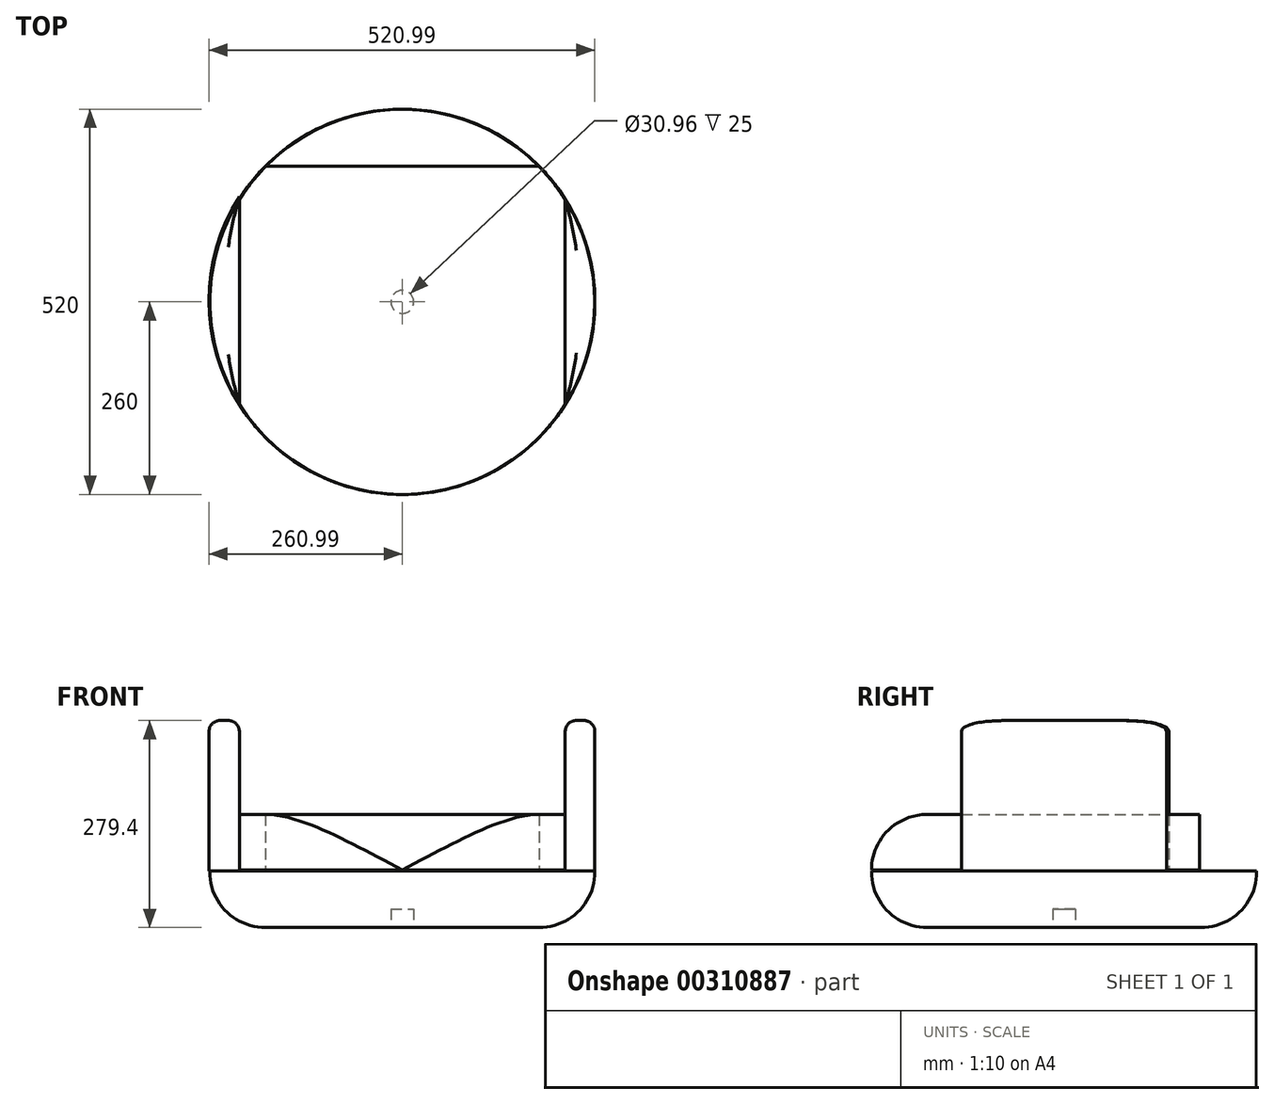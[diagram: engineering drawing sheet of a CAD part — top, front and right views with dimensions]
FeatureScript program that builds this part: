
annotation { "Feature Type Name" : "Feature", "Feature Type Description" : "" }
export const myFeature = defineFeature(function(context is Context, id is Id, definition is map)
    precondition{}
    {
        {
            var Q0;
            Q0=qCreatedBy(makeId("Front.planeOp"),FACE);
            var sketch = newSketch(context, id + "F0", { "sketchPlane" : qUnion([Q0])});
            skLineSegment(sketch, "E0.bottom", {"start": v(260, 38.1) * mm, "end": v(0, 38.1) * mm});
            skLineSegment(sketch, "E0.top", {"start": v(185, -38.1) * mm, "end": v(0, -38.1) * mm});
            skLineSegment(sketch, "E0.left", {"start": v(260, 38.1) * mm, "end": v(260, 36.9) * mm});
            skLineSegment(sketch, "E0.right", {"start": v(-260, 38.1) * mm, "end": v(-260, 36.9) * mm});
            skPoint(sketch, "E0.middle", {"position": v(0, 0) * mm});
            skPoint(sketch, "E1.visualSharp", {"position": v(260, -38.1) * mm});
            skArc(sketch, "E1.filletArc", {"start": v(185, -38.1) * mm, "mid": v(238.03, -16.13) * mm, "end": v(260, 36.9) * mm});
            skPoint(sketch, "E2.visualSharp", {"position": v(-260, -38.1) * mm});
            skLineSegment(sketch, "E3", {"start": v(0, 38.1) * mm, "end": v(0, -38.1) * mm});
            skPoint(sketch, "E2.filletArc.end.orphan", {"position": v(-185, -38.1) * mm});
            skSolve(sketch);
        }
        {
            var Q0;
            Q0=makeQuery(id+"F0.imprint","IMPRINT",FACE,{"disambiguationData":[TD([[makeQuery(id+"F0.imprint","IMPRINT",EDGE,{"derivedFrom":sQuery(id+"F0.wireOp",EDGE,"E0.bottom")}),1.0]])]});
            var Q1;
            Q1=sQuery(id+"F0.wireOp",EDGE,"E3");
            revolve(context, id + "F1", {"entities" : qUnion([Q0]), "axis" : qUnion([Q1]), "revolveType" : RevolveType.FULL});
        }
        {
            var Q0;
            Q0=qCreatedBy(makeId("Right.planeOp"),FACE);
            var sketch = newSketch(context, id + "F2", { "sketchPlane" : qUnion([Q0])});
            skLineSegment(sketch, "E4.bottom", {"start": v(0, 38.2) * mm, "end": v(260, 38.2) * mm});
            skLineSegment(sketch, "E4.top", {"start": v(0, 114.4) * mm, "end": v(185, 114.4) * mm});
            skLineSegment(sketch, "E4.right", {"start": v(260, 38.2) * mm, "end": v(260, 39.4) * mm});
            skPoint(sketch, "E5.visualSharp", {"position": v(260, 114.4) * mm});
            skArc(sketch, "E5.filletArc", {"start": v(260, 39.4) * mm, "mid": v(238.03, 92.43) * mm, "end": v(185, 114.4) * mm});
            skLineSegment(sketch, "E6.MirrorCS", {"start": v(0, 114.4) * mm, "end": v(-185, 114.4) * mm});
            skArc(sketch, "E7.MirrorCS", {"start": v(-260, 39.4) * mm, "mid": v(-238.03, 92.43) * mm, "end": v(-185, 114.4) * mm});
            skLineSegment(sketch, "E8.MirrorCS", {"start": v(0, 38.2) * mm, "end": v(-260, 38.2) * mm});
            skLineSegment(sketch, "E9", {"start": v(-260, 39.4) * mm, "end": v(260, 39.4) * mm});
            skSolve(sketch);
        }
        {
            var Q0;
            Q0=makeQuery(id+"F2.imprint","IMPRINT",FACE,{"disambiguationData":[TD([[makeQuery(id+"F2.imprint","IMPRINT",EDGE,{"derivedFrom":sQuery(id+"F2.wireOp",EDGE,"E4.top")}),-1.0]])]});
            extrude(context, id + "F3", {"entities" : qUnion([Q0]), "endBound" : BoundingType.SYMMETRIC, "depth" : 440 * mm});
        }
        {
            var Q0;
            Q0=qCreatedBy(makeId("Top.planeOp"),FACE);
            var sketch = newSketch(context, id + "F4", { "sketchPlane" : qUnion([Q0])});
            skCircle(sketch, "E10", {"center": v(0, 0) * mm, "radius": 260 * mm});
            skCircle(sketch, "E11", {"center": v(0, 0) * mm, "radius": 500 * mm});
            skSolve(sketch);
        }
        {
            var Q0;
            Q0=makeQuery(id+"F4.imprint","IMPRINT",FACE,{"disambiguationData":[TD([[makeQuery(id+"F4.imprint","IMPRINT",EDGE,{"derivedFrom":sQuery(id+"F4.wireOp",EDGE,"E10")}),-1.0]])]});
            extrude(context, id + "F5", {"entities" : qUnion([Q0]), "operationType" : NewBodyOperationType.REMOVE, "depth" : 500 * mm});
        }
        {
            var Q0;
            Q0=makeQuery(id+"F1.opRevolve","SWEPT_FACE",FACE,{"disambiguationData":[OSD([sQuery(id+"F0.wireOp",EDGE,"E0.bottom")])]});
            var sketch = newSketch(context, id + "F6", { "sketchPlane" : qUnion([Q0])});
            skPoint(sketch, "E12", {"position": v(-220, 141.68) * mm});
            skPoint(sketch, "E13", {"position": v(-220, -138.56) * mm});
            skPoint(sketch, "E14", {"position": v(220, -138.56) * mm});
            skPoint(sketch, "E15", {"position": v(220, 138.56) * mm});
            skArc(sketch, "E16", {"start": v(220, -138.56) * mm, "mid": v(260, 0) * mm, "end": v(220, 138.56) * mm});
            skArc(sketch, "E17", {"start": v(-220, 141.68) * mm, "mid": v(-260.99, 1.56) * mm, "end": v(-220, -138.56) * mm});
            skLineSegment(sketch, "E18", {"start": v(220, 138.56) * mm, "end": v(220, -138.56) * mm});
            skLineSegment(sketch, "E19", {"start": v(-220, 141.68) * mm, "end": v(-220, -138.56) * mm});
            skSolve(sketch);
        }
        {
            var Q0;
            Q0 = qSketchRegion(id + "F6", true);
            extrude(context, id + "F7", {"entities" : qUnion([Q0]), "depth" : 203.2 * mm});
        }
        {
            var Q0;
            Q0=makeQuery(id+"F7.opExtrude","CAP_FACE",FACE,{"disambiguationData":[OSD([sQuery(id+"F6.wireOp",EDGE,"E16"),sQuery(id+"F6.wireOp",EDGE,"E18")])],"isStart":false});
            fillet(context, id + "F8", {"entities" : qUnion([Q0]), "radius" : 15 * mm, "tangentPropagation" : true, "allowEdgeOverflow" : false});
        }
        {
            var Q0;
            Q0=makeQuery(id+"F7.opExtrude","CAP_FACE",FACE,{"disambiguationData":[OSD([sQuery(id+"F6.wireOp",EDGE,"E17"),sQuery(id+"F6.wireOp",EDGE,"E19")])],"isStart":false});
            fillet(context, id + "F9", {"entities" : qUnion([Q0]), "radius" : 15 * mm, "tangentPropagation" : true, "allowEdgeOverflow" : false});
        }
        {
            var Q0;
            Q0=makeQuery(id+"F1.opRevolve","SWEPT_FACE",FACE,{"disambiguationData":[OSD([sQuery(id+"F0.wireOp",EDGE,"E0.top")])]});
            var sketch = newSketch(context, id + "F10", { "sketchPlane" : qUnion([Q0])});
            skCircle(sketch, "E20", {"center": v(0, 0) * mm, "radius": 15.48 * mm});
            skSolve(sketch);
        }
        {
            var Q0;
            Q0=makeQuery(id+"F10.imprint","IMPRINT",FACE,{"disambiguationData":[TD([[makeQuery(id+"F10.imprint","IMPRINT",EDGE,{"derivedFrom":sQuery(id+"F10.wireOp",EDGE,"E20")}),1.0]])]});
            var Q1;
            Q1=sQuery(id+"F10.wireOp",EDGE,"E20");
            extrude(context, id + "F11", {"entities" : qUnion([Q0]), "operationType" : NewBodyOperationType.REMOVE, "surfaceEntities" : qUnion([Q1]), "oppositeDirection" : true, "depth" : 25 * mm});
        }
        {
            var Q0;
            Q0=makeQuery(id+"F10.imprint","IMPRINT",FACE,{"disambiguationData":[TD([[makeQuery(id+"F10.imprint","IMPRINT",EDGE,{"derivedFrom":sQuery(id+"F10.wireOp",EDGE,"E20")}),1.0]])]});
            var Q1;
            Q1=sQuery(id+"F10.wireOp",EDGE,"E20");
            extrude(context, id + "F12", {"entities" : qUnion([Q0]), "operationType" : NewBodyOperationType.REMOVE, "surfaceEntities" : qUnion([Q1]), "oppositeDirection" : true, "depth" : 25 * mm});
        }
        {
            var Q0;
            Q0=qCreatedBy(makeId("Right.planeOp"),FACE);
            var sketch = newSketch(context, id + "F13", { "sketchPlane" : qUnion([Q0])});
            skLineSegment(sketch, "E21.bottom", {"start": v(182.89, 114.47) * mm, "end": v(271.69, 114.47) * mm});
            skLineSegment(sketch, "E21.top", {"start": v(182.89, 39.26) * mm, "end": v(271.69, 39.26) * mm});
            skLineSegment(sketch, "E21.left", {"start": v(182.89, 114.47) * mm, "end": v(182.89, 39.26) * mm});
            skLineSegment(sketch, "E21.right", {"start": v(271.69, 114.47) * mm, "end": v(271.69, 39.26) * mm});
            skSolve(sketch);
        }
        {
            var Q0;
            Q0=makeQuery(id+"F13.imprint","IMPRINT",FACE,{"disambiguationData":[TD([[makeQuery(id+"F13.imprint","IMPRINT",EDGE,{"derivedFrom":sQuery(id+"F13.wireOp",EDGE,"E21.bottom")}),-1.0]])]});
            extrude(context, id + "F14", {"entities" : qUnion([Q0]), "operationType" : NewBodyOperationType.REMOVE, "endBound" : BoundingType.SYMMETRIC, "depth" : 900 * mm});
        }
    });
